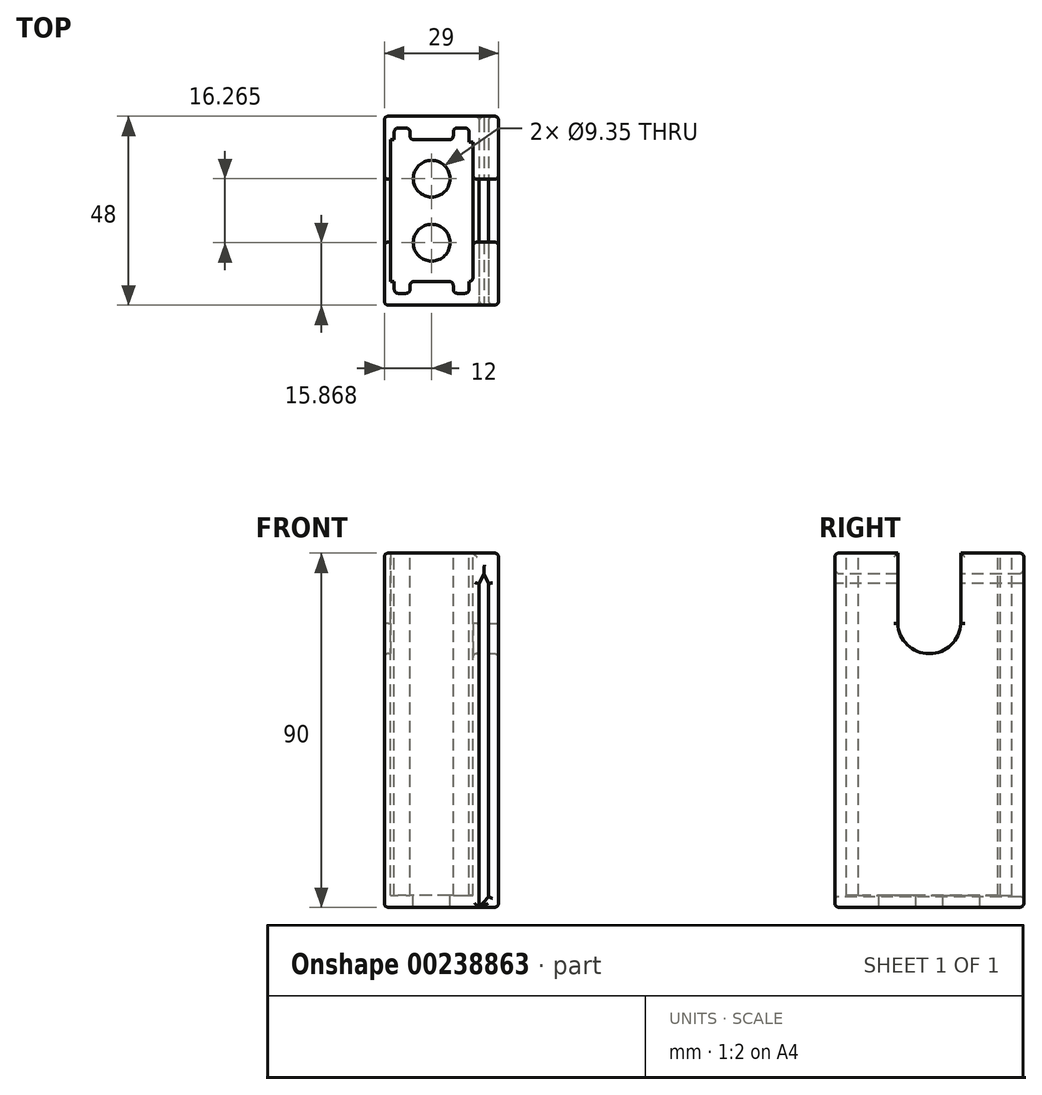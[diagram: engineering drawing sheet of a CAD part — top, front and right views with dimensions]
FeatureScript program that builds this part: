
annotation { "Feature Type Name" : "Feature", "Feature Type Description" : "" }
export const myFeature = defineFeature(function(context is Context, id is Id, definition is map)
    precondition{}
    {
        {
            var Q0;
            Q0=qCreatedBy(makeId("Right.planeOp"),FACE);
            var sketch = newSketch(context, id + "F0", { "sketchPlane" : qUnion([Q0])});
            skLineSegment(sketch, "E0", {"start": v(0, 0) * mm, "end": v(0, 45) * mm});
            skLineSegment(sketch, "E1", {"start": v(0, 45) * mm, "end": v(-24, 45) * mm});
            skLineSegment(sketch, "E2", {"start": v(-24, 45) * mm, "end": v(-24, 0) * mm});
            skLineSegment(sketch, "E3.MirrorCS", {"start": v(0, 45) * mm, "end": v(24, 45) * mm});
            skLineSegment(sketch, "E4.MirrorCS", {"start": v(24, 45) * mm, "end": v(24, 0) * mm});
            skLineSegment(sketch, "E5.MirrorCS", {"start": v(-24, -45) * mm, "end": v(-24, 0) * mm});
            skLineSegment(sketch, "E6.MirrorCS", {"start": v(0, -45) * mm, "end": v(-24, -45) * mm});
            skLineSegment(sketch, "E7.MirrorCS", {"start": v(0, -45) * mm, "end": v(24, -45) * mm});
            skLineSegment(sketch, "E8.MirrorCS", {"start": v(24, -45) * mm, "end": v(24, 0) * mm});
            skSolve(sketch);
        }
        {
            var Q0;
            Q0=makeQuery(id+"F0.imprint","IMPRINT",FACE,{"disambiguationData":[TD([[makeQuery(id+"F0.imprint","IMPRINT",EDGE,{"derivedFrom":sQuery(id+"F0.wireOp",EDGE,"E1")}),1.0]])]});
            extrude(context, id + "F1", {"entities" : qUnion([Q0]), "depth" : 24 * mm, "offsetDistance" : 25.4 * mm});
        }
        {
            var Q0;
            Q0=makeQuery(id+"F1.opExtrude","SWEPT_FACE",FACE,{"disambiguationData":[OSD([sQuery(id+"F0.wireOp",EDGE,"E1"),sQuery(id+"F0.wireOp",EDGE,"E3.MirrorCS")])]});
            var sketch = newSketch(context, id + "F2", { "sketchPlane" : qUnion([Q0])});
            skLineSegment(sketch, "E9", {"start": v(0, 10.58) * mm, "end": v(1.5, 10.58) * mm});
            skLineSegment(sketch, "E10", {"start": v(24, 10.58) * mm, "end": v(22.5, 10.58) * mm});
            skLineSegment(sketch, "E11", {"start": v(1.5, 0) * mm, "end": v(1.5, 18) * mm});
            skPoint(sketch, "E11.startSnap0", {"position": v(0, 0) * mm});
            skLineSegment(sketch, "E12.MirrorCS", {"start": v(1.5, 0) * mm, "end": v(1.5, -18) * mm});
            skLineSegment(sketch, "E13", {"start": v(1.5, 18) * mm, "end": v(22.5, 18) * mm});
            skLineSegment(sketch, "E14", {"start": v(22.5, 18) * mm, "end": v(22.5, -18) * mm});
            skLineSegment(sketch, "E15", {"start": v(22.5, -18) * mm, "end": v(1.5, -18) * mm});
            skLineSegment(sketch, "E16", {"start": v(22.5, 18) * mm, "end": v(20.97, 18) * mm});
            skLineSegment(sketch, "E17", {"start": v(22.5, 17.44) * mm, "end": v(21.5, 17.44) * mm});
            skLineSegment(sketch, "E18", {"start": v(21.5, 17.44) * mm, "end": v(17.5, 17.44) * mm});
            skLineSegment(sketch, "E19.MirrorCS", {"start": v(21.5, -17.44) * mm, "end": v(17.5, -17.44) * mm});
            skLineSegment(sketch, "E20", {"start": v(12, 18) * mm, "end": v(12, 7.15) * mm});
            skLineSegment(sketch, "E21.MirrorCS", {"start": v(2.5, -17.44) * mm, "end": v(6.5, -17.44) * mm});
            skLineSegment(sketch, "E22.MirrorCS", {"start": v(2.5, 17.44) * mm, "end": v(6.5, 17.44) * mm});
            skLineSegment(sketch, "E23", {"start": v(2.5, 0) * mm, "end": v(2.5, 21) * mm});
            skLineSegment(sketch, "E24", {"start": v(6.5, 18) * mm, "end": v(6.5, 21) * mm});
            skLineSegment(sketch, "E25", {"start": v(6.5, 21) * mm, "end": v(2.5, 21) * mm});
            skLineSegment(sketch, "E26.MirrorCS", {"start": v(21.5, 0) * mm, "end": v(21.5, 21) * mm});
            skLineSegment(sketch, "E27.MirrorCS", {"start": v(17.5, 21) * mm, "end": v(21.5, 21) * mm});
            skLineSegment(sketch, "E28.MirrorCS", {"start": v(17.5, 18) * mm, "end": v(17.5, 21) * mm});
            skLineSegment(sketch, "E29.MirrorCS", {"start": v(6.5, -21) * mm, "end": v(2.5, -21) * mm});
            skLineSegment(sketch, "E30.MirrorCS", {"start": v(6.5, -18) * mm, "end": v(6.5, -21) * mm});
            skLineSegment(sketch, "E31.MirrorCS", {"start": v(2.5, 0) * mm, "end": v(2.5, -21) * mm});
            skLineSegment(sketch, "E32.MirrorCS", {"start": v(17.5, -21) * mm, "end": v(21.5, -21) * mm});
            skLineSegment(sketch, "E33.MirrorCS", {"start": v(17.5, -18) * mm, "end": v(17.5, -21) * mm});
            skLineSegment(sketch, "E34.MirrorCS", {"start": v(21.5, 0) * mm, "end": v(21.5, -21) * mm});
            skSolve(sketch);
        }
        {
            var Q0;
            {var subQ0=sQuery(id+"F2.wireOp",EDGE,"E24");Q0=makeQuery(id+"F2.imprint","IMPRINT",FACE,{"disambiguationData":[TD([[makeQuery(id+"F2.imprint","IMPRINT",EDGE,{"derivedFrom":subQ0}),1.0]])]});}
            var Q1;
            {var subQ0=sQuery(id+"F2.wireOp",EDGE,"E27.MirrorCS");Q1=makeQuery(id+"F2.imprint","IMPRINT",FACE,{"disambiguationData":[TD([[makeQuery(id+"F2.imprint","IMPRINT",EDGE,{"derivedFrom":subQ0}),-1.0]])]});}
            var Q2;
            {var subQ2=sQuery(id+"F2.wireOp",EDGE,"E13");var subQ16=makeQuery(id+"F2.imprint","IMPRINT",VERTEX,{"derivedFrom":subQ2});Q2=makeQuery(id+"F2.imprint","IMPRINT",FACE,{"disambiguationData":[TD([[makeQuery(id+"F2.imprint","IMPRINT",EDGE,{"disambiguationData":[TD([[subQ16,1.0]])],"derivedFrom":subQ2}),-1.0]])]});}
            var Q3;
            {var subQ5=sQuery(id+"F2.wireOp",EDGE,"E12.MirrorCS");Q3=makeQuery(id+"F2.imprint","IMPRINT",FACE,{"disambiguationData":[TD([[makeQuery(id+"F2.imprint","IMPRINT",EDGE,{"derivedFrom":subQ5}),1.0]])]});}
            var Q4;
            {var subQ0=sQuery(id+"F2.wireOp",EDGE,"E17");Q4=makeQuery(id+"F2.imprint","IMPRINT",FACE,{"disambiguationData":[TD([[makeQuery(id+"F2.imprint","IMPRINT",EDGE,{"derivedFrom":subQ0}),1.0]])]});}
            var Q5;
            {var subQ4=sQuery(id+"F2.wireOp",EDGE,"E32.MirrorCS");Q5=makeQuery(id+"F2.imprint","IMPRINT",FACE,{"disambiguationData":[TD([[makeQuery(id+"F2.imprint","IMPRINT",EDGE,{"derivedFrom":subQ4}),1.0]])]});}
            var Q6;
            {var subQ4=sQuery(id+"F2.wireOp",EDGE,"E29.MirrorCS");Q6=makeQuery(id+"F2.imprint","IMPRINT",FACE,{"disambiguationData":[TD([[makeQuery(id+"F2.imprint","IMPRINT",EDGE,{"derivedFrom":subQ4}),-1.0]])]});}
            extrude(context, id + "F3", {"entities" : qUnion([Q0, Q1, Q2, Q3, Q4, Q5, Q6]), "operationType" : NewBodyOperationType.REMOVE, "oppositeDirection" : true, "depth" : 87 * mm, "offsetDistance" : 25.4 * mm});
        }
        {
            var Q0;
            Q0=makeQuery(id+"F1.opExtrude","CAP_FACE",FACE,{"disambiguationData":[OSD([sQuery(id+"F0.wireOp",EDGE,"E1"),sQuery(id+"F0.wireOp",EDGE,"E2"),sQuery(id+"F0.wireOp",EDGE,"E3.MirrorCS"),sQuery(id+"F0.wireOp",EDGE,"E4.MirrorCS"),sQuery(id+"F0.wireOp",EDGE,"E5.MirrorCS"),sQuery(id+"F0.wireOp",EDGE,"E6.MirrorCS"),sQuery(id+"F0.wireOp",EDGE,"E7.MirrorCS"),sQuery(id+"F0.wireOp",EDGE,"E8.MirrorCS")])],"isStart":false});
            var sketch = newSketch(context, id + "F4", { "sketchPlane" : qUnion([Q0])});
            skLineSegment(sketch, "E35", {"start": v(0, 45) * mm, "end": v(0, 27.46) * mm});
            skLineSegment(sketch, "E36", {"start": v(0, 45) * mm, "end": v(-8, 45) * mm});
            skLineSegment(sketch, "E37", {"start": v(-8, 45) * mm, "end": v(-8, 27.14) * mm});
            skCircle(sketch, "E38", {"center": v(0, 27.46) * mm, "radius": 8 * mm});
            skLineSegment(sketch, "E39.MirrorCS", {"start": v(0, 45) * mm, "end": v(8, 45) * mm});
            skLineSegment(sketch, "E40.MirrorCS", {"start": v(8, 45) * mm, "end": v(8, 27.14) * mm});
            skSolve(sketch);
        }
        {
            var Q0;
            {var subQ0=sQuery(id+"F4.wireOp",EDGE,"E39.MirrorCS");Q0=makeQuery(id+"F4.imprint","IMPRINT",FACE,{"disambiguationData":[TD([[makeQuery(id+"F4.imprint","IMPRINT",EDGE,{"derivedFrom":subQ0}),-1.0]])]});}
            var Q1;
            {var subQ0=sQuery(id+"F4.wireOp",EDGE,"E36");Q1=makeQuery(id+"F4.imprint","IMPRINT",FACE,{"disambiguationData":[TD([[makeQuery(id+"F4.imprint","IMPRINT",EDGE,{"derivedFrom":subQ0}),-1.0]])]});}
            var Q2;
            {var subQ0=sQuery(id+"F4.wireOp",EDGE,"E38");var subQ1=sQuery(id+"F4.wireOp",EDGE,"E37");var subQ2=makeQuery(id+"F4.imprint","INTERSECT",VERTEX,{"disambiguationData":[OD(0.0)],"derivedFrom":[subQ1,subQ0]});Q2=makeQuery(id+"F4.imprint","IMPRINT",FACE,{"disambiguationData":[TD([[makeQuery(id+"F4.imprint","IMPRINT",EDGE,{"disambiguationData":[TD([[subQ2,1.0]])],"derivedFrom":subQ1}),1.0]])]});}
            extrude(context, id + "F5", {"entities" : qUnion([Q0, Q1, Q2]), "operationType" : NewBodyOperationType.REMOVE, "oppositeDirection" : true, "depth" : 25.4 * mm, "offsetDistance" : 25.4 * mm});
        }
        {
            var Q0;
            Q0=makeQuery(id+"F1.opExtrude","CAP_FACE",FACE,{"disambiguationData":[OSD([sQuery(id+"F0.wireOp",EDGE,"E1"),sQuery(id+"F0.wireOp",EDGE,"E2"),sQuery(id+"F0.wireOp",EDGE,"E3.MirrorCS"),sQuery(id+"F0.wireOp",EDGE,"E4.MirrorCS"),sQuery(id+"F0.wireOp",EDGE,"E5.MirrorCS"),sQuery(id+"F0.wireOp",EDGE,"E6.MirrorCS"),sQuery(id+"F0.wireOp",EDGE,"E7.MirrorCS"),sQuery(id+"F0.wireOp",EDGE,"E8.MirrorCS")])],"isStart":false});
            extrude(context, id + "F6", {"entities" : qUnion([Q0]), "operationType" : NewBodyOperationType.ADD, "depth" : 5 * mm, "offsetDistance" : 25.4 * mm});
        }
        {
            var Q0;
            {var subQ0=sQuery(id+"F0.wireOp",EDGE,"E5.MirrorCS");var subQ1=sQuery(id+"F0.wireOp",EDGE,"E2");Q0=makeQuery(id+"F6.boolean.opBoolean","MERGE",FACE,{"derivedFrom":[makeQuery(id+"F1.opExtrude","SWEPT_FACE",FACE,{"disambiguationData":[OSD([subQ1,subQ0])]}),makeQuery(id+"F6.opExtrude","SWEPT_FACE",FACE,{"disambiguationData":[OSD([subQ1,subQ0])]})]});}
            var sketch = newSketch(context, id + "F7", { "sketchPlane" : qUnion([Q0])});
            skLineSegment(sketch, "E41", {"start": v(29, 37.24) * mm, "end": v(24, 37.24) * mm});
            skLineSegment(sketch, "E42", {"start": v(24, 37.24) * mm, "end": v(24, -45) * mm});
            skLineSegment(sketch, "E43", {"start": v(26.5, 37.24) * mm, "end": v(26.5, -45) * mm});
            skLineSegment(sketch, "E44", {"start": v(24.09, -45) * mm, "end": v(26.5, -42.37) * mm});
            skLineSegment(sketch, "E45", {"start": v(25.33, 39.72) * mm, "end": v(24, 37.24) * mm});
            skLineSegment(sketch, "E46", {"start": v(25.33, 39.72) * mm, "end": v(26.5, 37.24) * mm});
            skSolve(sketch);
        }
        {
            var Q0;
            {var subQ4=sQuery(id+"F7.wireOp",EDGE,"E42");Q0=makeQuery(id+"F7.imprint","IMPRINT",FACE,{"disambiguationData":[TD([[makeQuery(id+"F7.imprint","IMPRINT",EDGE,{"derivedFrom":subQ4}),1.0]])]});}
            var Q1;
            {var subQ0=sQuery(id+"F7.wireOp",EDGE,"E45");Q1=makeQuery(id+"F7.imprint","IMPRINT",FACE,{"disambiguationData":[TD([[makeQuery(id+"F7.imprint","IMPRINT",EDGE,{"derivedFrom":subQ0}),1.0]])]});}
            extrude(context, id + "F8", {"entities" : qUnion([Q0, Q1]), "operationType" : NewBodyOperationType.REMOVE, "oppositeDirection" : true, "depth" : 127 * mm, "offsetDistance" : 25.4 * mm});
        }
        {
            var Q0;
            Q0=makeQuery(id+"F6.opExtrude","CAP_EDGE",EDGE,{"disambiguationData":[OSD([sQuery(id+"F0.wireOp",EDGE,"E4.MirrorCS"),sQuery(id+"F0.wireOp",EDGE,"E8.MirrorCS")])],"isStart":false});
            var Q1;
            Q1=makeQuery(id+"F6.opExtrude","CAP_EDGE",EDGE,{"disambiguationData":[OSD([sQuery(id+"F0.wireOp",EDGE,"E2"),sQuery(id+"F0.wireOp",EDGE,"E5.MirrorCS")])],"isStart":false});
            var Q2;
            Q2=makeQuery(id+"F6.opExtrude","CAP_FACE",FACE,{"disambiguationData":[OSD([sQuery(id+"F0.wireOp",EDGE,"E1"),sQuery(id+"F0.wireOp",EDGE,"E2"),sQuery(id+"F0.wireOp",EDGE,"E3.MirrorCS"),sQuery(id+"F0.wireOp",EDGE,"E4.MirrorCS"),sQuery(id+"F0.wireOp",EDGE,"E5.MirrorCS"),sQuery(id+"F0.wireOp",EDGE,"E6.MirrorCS"),sQuery(id+"F0.wireOp",EDGE,"E7.MirrorCS"),sQuery(id+"F0.wireOp",EDGE,"E8.MirrorCS")])],"isStart":false});
            var Q3;
            {var subQ0=sQuery(id+"F0.wireOp",EDGE,"E8.MirrorCS");var subQ1=sQuery(id+"F0.wireOp",EDGE,"E4.MirrorCS");Q3=makeQuery(id+"F6.boolean.opBoolean","MERGE",FACE,{"derivedFrom":[makeQuery(id+"F1.opExtrude","SWEPT_FACE",FACE,{"disambiguationData":[OSD([subQ1,subQ0])]}),makeQuery(id+"F6.opExtrude","SWEPT_FACE",FACE,{"disambiguationData":[OSD([subQ1,subQ0])]})]});}
            var Q4;
            Q4=makeQuery(id+"F1.opExtrude","CAP_FACE",FACE,{"disambiguationData":[OSD([sQuery(id+"F0.wireOp",EDGE,"E1"),sQuery(id+"F0.wireOp",EDGE,"E2"),sQuery(id+"F0.wireOp",EDGE,"E3.MirrorCS"),sQuery(id+"F0.wireOp",EDGE,"E4.MirrorCS"),sQuery(id+"F0.wireOp",EDGE,"E5.MirrorCS"),sQuery(id+"F0.wireOp",EDGE,"E6.MirrorCS"),sQuery(id+"F0.wireOp",EDGE,"E7.MirrorCS"),sQuery(id+"F0.wireOp",EDGE,"E8.MirrorCS")])],"isStart":true});
            var Q5;
            {var subQ0=sQuery(id+"F0.wireOp",EDGE,"E5.MirrorCS");var subQ1=sQuery(id+"F0.wireOp",EDGE,"E2");Q5=makeQuery(id+"F6.boolean.opBoolean","MERGE",FACE,{"derivedFrom":[makeQuery(id+"F1.opExtrude","SWEPT_FACE",FACE,{"disambiguationData":[OSD([subQ1,subQ0])]}),makeQuery(id+"F6.opExtrude","SWEPT_FACE",FACE,{"disambiguationData":[OSD([subQ1,subQ0])]})]});}
            var Q6;
            Q6=makeQuery(id+"F3.boolean.opBoolean","COPY",EDGE,{"derivedFrom":makeQuery(id+"F3.opExtrude","SWEPT_EDGE",EDGE,{"disambiguationData":[OSD([sQuery(id+"F2.wireOp",EDGE,"E26.MirrorCS"),sQuery(id+"F2.wireOp",EDGE,"E27.MirrorCS")])]})});
            var Q7;
            Q7=makeQuery(id+"F3.boolean.opBoolean","COPY",EDGE,{"derivedFrom":makeQuery(id+"F3.opExtrude","SWEPT_EDGE",EDGE,{"disambiguationData":[OSD([sQuery(id+"F2.wireOp",EDGE,"E27.MirrorCS"),sQuery(id+"F2.wireOp",EDGE,"E28.MirrorCS")])]})});
            var Q8;
            Q8=makeQuery(id+"F3.boolean.opBoolean","COPY",EDGE,{"derivedFrom":makeQuery(id+"F3.opExtrude","SWEPT_EDGE",EDGE,{"disambiguationData":[OSD([sQuery(id+"F2.wireOp",EDGE,"E23"),sQuery(id+"F2.wireOp",EDGE,"E25")])]})});
            var Q9;
            Q9=makeQuery(id+"F3.boolean.opBoolean","COPY",EDGE,{"derivedFrom":makeQuery(id+"F3.opExtrude","SWEPT_EDGE",EDGE,{"disambiguationData":[OSD([sQuery(id+"F2.wireOp",EDGE,"E24"),sQuery(id+"F2.wireOp",EDGE,"E25")])]})});
            var Q10;
            Q10=makeQuery(id+"F3.boolean.opBoolean","COPY",EDGE,{"derivedFrom":makeQuery(id+"F3.opExtrude","SWEPT_EDGE",EDGE,{"disambiguationData":[OSD([sQuery(id+"F2.wireOp",EDGE,"E13"),sQuery(id+"F2.wireOp",EDGE,"E28.MirrorCS")])]})});
            var Q11;
            Q11=makeQuery(id+"F3.boolean.opBoolean","COPY",EDGE,{"derivedFrom":makeQuery(id+"F3.opExtrude","SWEPT_EDGE",EDGE,{"disambiguationData":[OSD([sQuery(id+"F2.wireOp",EDGE,"E13"),sQuery(id+"F2.wireOp",EDGE,"E24")])]})});
            var Q12;
            Q12=makeQuery(id+"F3.boolean.opBoolean","COPY",EDGE,{"derivedFrom":makeQuery(id+"F3.opExtrude","SWEPT_EDGE",EDGE,{"disambiguationData":[OSD([sQuery(id+"F2.wireOp",EDGE,"E32.MirrorCS"),sQuery(id+"F2.wireOp",EDGE,"E34.MirrorCS")])]})});
            var Q13;
            Q13=makeQuery(id+"F3.boolean.opBoolean","COPY",EDGE,{"derivedFrom":makeQuery(id+"F3.opExtrude","SWEPT_EDGE",EDGE,{"disambiguationData":[OSD([sQuery(id+"F2.wireOp",EDGE,"E14"),sQuery(id+"F2.wireOp",EDGE,"E15")])]})});
            var Q14;
            Q14=makeQuery(id+"F3.boolean.opBoolean","COPY",EDGE,{"derivedFrom":makeQuery(id+"F3.opExtrude","SWEPT_EDGE",EDGE,{"disambiguationData":[OSD([sQuery(id+"F2.wireOp",EDGE,"E15"),sQuery(id+"F2.wireOp",EDGE,"E33.MirrorCS")])]})});
            var Q15;
            Q15=makeQuery(id+"F3.boolean.opBoolean","COPY",EDGE,{"derivedFrom":makeQuery(id+"F3.opExtrude","SWEPT_EDGE",EDGE,{"disambiguationData":[OSD([sQuery(id+"F2.wireOp",EDGE,"E32.MirrorCS"),sQuery(id+"F2.wireOp",EDGE,"E33.MirrorCS")])]})});
            var Q16;
            Q16=makeQuery(id+"F3.boolean.opBoolean","COPY",EDGE,{"derivedFrom":makeQuery(id+"F3.opExtrude","SWEPT_EDGE",EDGE,{"disambiguationData":[OSD([sQuery(id+"F2.wireOp",EDGE,"E15"),sQuery(id+"F2.wireOp",EDGE,"E30.MirrorCS")])]})});
            var Q17;
            Q17=makeQuery(id+"F3.boolean.opBoolean","COPY",EDGE,{"derivedFrom":makeQuery(id+"F3.opExtrude","SWEPT_EDGE",EDGE,{"disambiguationData":[OSD([sQuery(id+"F2.wireOp",EDGE,"E29.MirrorCS"),sQuery(id+"F2.wireOp",EDGE,"E30.MirrorCS")])]})});
            var Q18;
            Q18=makeQuery(id+"F3.boolean.opBoolean","COPY",EDGE,{"derivedFrom":makeQuery(id+"F3.opExtrude","SWEPT_EDGE",EDGE,{"disambiguationData":[OSD([sQuery(id+"F2.wireOp",EDGE,"E29.MirrorCS"),sQuery(id+"F2.wireOp",EDGE,"E31.MirrorCS")])]})});
            var Q19;
            {var subQ0=sQuery(id+"F2.wireOp",EDGE,"E15");Q19=makeQuery(id+"F3.boolean.opBoolean","COPY",EDGE,{"derivedFrom":makeQuery(id+"F3.opExtrude","CAP_EDGE",EDGE,{"disambiguationData":[OSD([subQ0]),TDD([makeQuery(id+"F2.imprint","IMPRINT",EDGE,{"disambiguationData":[TD([[makeQuery(id+"F2.imprint","INTERSECT",VERTEX,{"derivedFrom":[subQ0,sQuery(id+"F2.wireOp",EDGE,"E30.MirrorCS")]}),1.0]])],"derivedFrom":subQ0})])],"isStart":true})});}
            var Q20;
            {var subQ0=sQuery(id+"F2.wireOp",EDGE,"E14");Q20=makeQuery(id+"F5.boolean.opBoolean","SPLIT",EDGE,{"disambiguationData":[TD([makeQuery(id+"F5.opExtrude","SWEPT_FACE",FACE,{"disambiguationData":[OSD([sQuery(id+"F4.wireOp",EDGE,"E37")])]})])],"derivedFrom":makeQuery(id+"F3.boolean.opBoolean","COPY",EDGE,{"derivedFrom":makeQuery(id+"F3.opExtrude","CAP_EDGE",EDGE,{"disambiguationData":[OSD([subQ0])],"isStart":true})})});}
            var Q21;
            Q21=makeQuery(id+"F3.boolean.opBoolean","COPY",EDGE,{"derivedFrom":makeQuery(id+"F3.opExtrude","CAP_EDGE",EDGE,{"disambiguationData":[OSD([sQuery(id+"F2.wireOp",EDGE,"E34.MirrorCS")])],"isStart":true})});
            var Q22;
            Q22=makeQuery(id+"F3.boolean.opBoolean","COPY",EDGE,{"derivedFrom":makeQuery(id+"F3.opExtrude","CAP_EDGE",EDGE,{"disambiguationData":[OSD([sQuery(id+"F2.wireOp",EDGE,"E33.MirrorCS")])],"isStart":true})});
            var Q23;
            Q23=makeQuery(id+"F3.boolean.opBoolean","COPY",EDGE,{"derivedFrom":makeQuery(id+"F3.opExtrude","CAP_EDGE",EDGE,{"disambiguationData":[OSD([sQuery(id+"F2.wireOp",EDGE,"E30.MirrorCS")])],"isStart":true})});
            var Q24;
            Q24=makeQuery(id+"F3.boolean.opBoolean","COPY",EDGE,{"derivedFrom":makeQuery(id+"F3.opExtrude","CAP_EDGE",EDGE,{"disambiguationData":[OSD([sQuery(id+"F2.wireOp",EDGE,"E31.MirrorCS")])],"isStart":true})});
            var Q25;
            Q25=makeQuery(id+"F3.boolean.opBoolean","COPY",EDGE,{"derivedFrom":makeQuery(id+"F3.opExtrude","CAP_EDGE",EDGE,{"disambiguationData":[OSD([sQuery(id+"F2.wireOp",EDGE,"E24")])],"isStart":true})});
            var Q26;
            Q26=makeQuery(id+"F3.boolean.opBoolean","COPY",EDGE,{"derivedFrom":makeQuery(id+"F3.opExtrude","CAP_EDGE",EDGE,{"disambiguationData":[OSD([sQuery(id+"F2.wireOp",EDGE,"E26.MirrorCS")])],"isStart":true})});
            var Q27;
            Q27=makeQuery(id+"F3.boolean.opBoolean","COPY",EDGE,{"derivedFrom":makeQuery(id+"F3.opExtrude","CAP_EDGE",EDGE,{"disambiguationData":[OSD([sQuery(id+"F2.wireOp",EDGE,"E28.MirrorCS")])],"isStart":true})});
            var Q28;
            Q28=makeQuery(id+"F3.boolean.opBoolean","COPY",EDGE,{"derivedFrom":makeQuery(id+"F3.opExtrude","CAP_EDGE",EDGE,{"disambiguationData":[OSD([sQuery(id+"F2.wireOp",EDGE,"E27.MirrorCS")])],"isStart":true})});
            var Q29;
            Q29=makeQuery(id+"F3.boolean.opBoolean","COPY",EDGE,{"derivedFrom":makeQuery(id+"F3.opExtrude","CAP_EDGE",EDGE,{"disambiguationData":[OSD([sQuery(id+"F2.wireOp",EDGE,"E25")])],"isStart":true})});
            var Q30;
            Q30=makeQuery(id+"F3.boolean.opBoolean","COPY",EDGE,{"derivedFrom":makeQuery(id+"F3.opExtrude","CAP_EDGE",EDGE,{"disambiguationData":[OSD([sQuery(id+"F2.wireOp",EDGE,"E23")])],"isStart":true})});
            var Q31;
            {var subQ0=sQuery(id+"F4.wireOp",EDGE,"E40.MirrorCS");var subQ1=sQuery(id+"F4.wireOp",EDGE,"E39.MirrorCS");var subQ2=sQuery(id+"F0.wireOp",EDGE,"E3.MirrorCS");var subQ3=sQuery(id+"F0.wireOp",EDGE,"E1");Q31=makeQuery(id+"F6.boolean.opBoolean","MERGE",EDGE,{"derivedFrom":[makeQuery(id+"F5.boolean.opBoolean","COPY",EDGE,{"disambiguationData":[TD([makeQuery(id+"F3.boolean.opBoolean","COPY",FACE,{"derivedFrom":makeQuery(id+"F3.opExtrude","SWEPT_FACE",FACE,{"disambiguationData":[OSD([sQuery(id+"F2.wireOp",EDGE,"E14")])]})})])],"derivedFrom":makeQuery(id+"F5.opExtrude","SWEPT_EDGE",EDGE,{"disambiguationData":[OSD([subQ3,subQ2,subQ1,subQ0])]})}),makeQuery(id+"F6.opExtrude","SWEPT_EDGE",EDGE,{"disambiguationData":[OSD([subQ3,subQ2,subQ1,subQ0])]})]});}
            var Q32;
            {var subQ0=sQuery(id+"F4.wireOp",EDGE,"E37");var subQ1=sQuery(id+"F4.wireOp",EDGE,"E36");var subQ2=sQuery(id+"F0.wireOp",EDGE,"E3.MirrorCS");var subQ3=sQuery(id+"F0.wireOp",EDGE,"E1");Q32=makeQuery(id+"F6.boolean.opBoolean","MERGE",EDGE,{"derivedFrom":[makeQuery(id+"F5.boolean.opBoolean","COPY",EDGE,{"disambiguationData":[TD([makeQuery(id+"F3.boolean.opBoolean","COPY",FACE,{"derivedFrom":makeQuery(id+"F3.opExtrude","SWEPT_FACE",FACE,{"disambiguationData":[OSD([sQuery(id+"F2.wireOp",EDGE,"E14")])]})})])],"derivedFrom":makeQuery(id+"F5.opExtrude","SWEPT_EDGE",EDGE,{"disambiguationData":[OSD([subQ3,subQ2,subQ1,subQ0])]})}),makeQuery(id+"F6.opExtrude","SWEPT_EDGE",EDGE,{"disambiguationData":[OSD([subQ3,subQ2,subQ1,subQ0])]})]});}
            var Q33;
            {var subQ0=sQuery(id+"F2.wireOp",EDGE,"E14");Q33=makeQuery(id+"F5.boolean.opBoolean","SPLIT",EDGE,{"disambiguationData":[TD([makeQuery(id+"F3.boolean.opBoolean","COPY",FACE,{"derivedFrom":makeQuery(id+"F3.opExtrude","SWEPT_FACE",FACE,{"disambiguationData":[OSD([sQuery(id+"F2.wireOp",EDGE,"E17")])]})})])],"derivedFrom":makeQuery(id+"F3.boolean.opBoolean","COPY",EDGE,{"derivedFrom":makeQuery(id+"F3.opExtrude","CAP_EDGE",EDGE,{"disambiguationData":[OSD([subQ0])],"isStart":true})})});}
            var Q34;
            Q34=makeQuery(id+"F5.boolean.opBoolean","INTERSECT",EDGE,{"derivedFrom":[makeQuery(id+"F3.boolean.opBoolean","COPY",FACE,{"derivedFrom":makeQuery(id+"F3.opExtrude","SWEPT_FACE",FACE,{"disambiguationData":[OSD([sQuery(id+"F2.wireOp",EDGE,"E14")])]})}),makeQuery(id+"F5.opExtrude","SWEPT_FACE",FACE,{"disambiguationData":[OSD([sQuery(id+"F4.wireOp",EDGE,"E40.MirrorCS")])]})]});
            var Q35;
            Q35=makeQuery(id+"F5.boolean.opBoolean","INTERSECT",EDGE,{"derivedFrom":[makeQuery(id+"F3.boolean.opBoolean","COPY",FACE,{"derivedFrom":makeQuery(id+"F3.opExtrude","SWEPT_FACE",FACE,{"disambiguationData":[OSD([sQuery(id+"F2.wireOp",EDGE,"E14")])]})}),makeQuery(id+"F5.opExtrude","SWEPT_FACE",FACE,{"disambiguationData":[OSD([sQuery(id+"F4.wireOp",EDGE,"E38")])]})]});
            var Q36;
            Q36=makeQuery(id+"F5.boolean.opBoolean","INTERSECT",EDGE,{"derivedFrom":[makeQuery(id+"F3.boolean.opBoolean","COPY",FACE,{"derivedFrom":makeQuery(id+"F3.opExtrude","SWEPT_FACE",FACE,{"disambiguationData":[OSD([sQuery(id+"F2.wireOp",EDGE,"E14")])]})}),makeQuery(id+"F5.opExtrude","SWEPT_FACE",FACE,{"disambiguationData":[OSD([sQuery(id+"F4.wireOp",EDGE,"E37")])]})]});
            fillet(context, id + "F9", {"entities" : qUnion([Q0, Q1, Q2, Q3, Q4, Q5, Q6, Q7, Q8, Q9, Q10, Q11, Q12, Q13, Q14, Q15, Q16, Q17, Q18, Q19, Q20, Q21, Q22, Q23, Q24, Q25, Q26, Q27, Q28, Q29, Q30, Q31, Q32, Q33, Q34, Q35, Q36]), "radius" : 1 * mm, "tangentPropagation" : true, "allowEdgeOverflow" : false});
        }
        {
            var Q0;
            Q0=makeQuery(id+"F3.boolean.opBoolean","COPY",FACE,{"derivedFrom":makeQuery(id+"F3.opExtrude","CAP_FACE",FACE,{"disambiguationData":[OSD([sQuery(id+"F2.wireOp",EDGE,"E11"),sQuery(id+"F2.wireOp",EDGE,"E12.MirrorCS"),sQuery(id+"F2.wireOp",EDGE,"E13"),sQuery(id+"F2.wireOp",EDGE,"E14"),sQuery(id+"F2.wireOp",EDGE,"E15"),sQuery(id+"F2.wireOp",EDGE,"E17"),sQuery(id+"F2.wireOp",EDGE,"E23"),sQuery(id+"F2.wireOp",EDGE,"E24"),sQuery(id+"F2.wireOp",EDGE,"E25"),sQuery(id+"F2.wireOp",EDGE,"E26.MirrorCS"),sQuery(id+"F2.wireOp",EDGE,"E27.MirrorCS"),sQuery(id+"F2.wireOp",EDGE,"E28.MirrorCS"),sQuery(id+"F2.wireOp",EDGE,"E29.MirrorCS"),sQuery(id+"F2.wireOp",EDGE,"E30.MirrorCS"),sQuery(id+"F2.wireOp",EDGE,"E31.MirrorCS"),sQuery(id+"F2.wireOp",EDGE,"E32.MirrorCS"),sQuery(id+"F2.wireOp",EDGE,"E33.MirrorCS"),sQuery(id+"F2.wireOp",EDGE,"E34.MirrorCS")])],"isStart":false})});
            var sketch = newSketch(context, id + "F10", { "sketchPlane" : qUnion([Q0])});
            skLineSegment(sketch, "E47", {"start": v(12, 18) * mm, "end": v(12, -20.67) * mm});
            skLineSegment(sketch, "E48", {"start": v(22.5, -7.82) * mm, "end": v(12, -7.82) * mm});
            skLineSegment(sketch, "E49", {"start": v(22.5, 8.13) * mm, "end": v(12, 8.13) * mm});
            skCircle(sketch, "E50", {"center": v(12, 8.13) * mm, "radius": 4.67 * mm});
            skCircle(sketch, "E51.MirrorC", {"center": v(12, -8.13) * mm, "radius": 4.67 * mm});
            skSolve(sketch);
        }
        {
            var Q0;
            {var subQ0=sQuery(id+"F10.wireOp",EDGE,"E47");var subQ1=makeQuery(id+"F10.imprint","INTERSECT",VERTEX,{"derivedFrom":[subQ0,sQuery(id+"F10.wireOp",EDGE,"E49")]});Q0=makeQuery(id+"F10.imprint","IMPRINT",FACE,{"disambiguationData":[TD([[makeQuery(id+"F10.imprint","IMPRINT",EDGE,{"disambiguationData":[TD([[subQ1,1.0]])],"derivedFrom":subQ0}),-1.0]])]});}
            var Q1;
            {var subQ0=sQuery(id+"F10.wireOp",EDGE,"E49");var subQ1=sQuery(id+"F10.wireOp",EDGE,"E47");var subQ2=makeQuery(id+"F10.imprint","INTERSECT",VERTEX,{"derivedFrom":[subQ1,subQ0]});Q1=makeQuery(id+"F10.imprint","IMPRINT",FACE,{"disambiguationData":[TD([[makeQuery(id+"F10.imprint","IMPRINT",EDGE,{"disambiguationData":[TD([[subQ2,-1.0]])],"derivedFrom":subQ1}),1.0]])]});}
            var Q2;
            {var subQ0=sQuery(id+"F10.wireOp",EDGE,"E49");var subQ1=sQuery(id+"F10.wireOp",EDGE,"E47");var subQ2=makeQuery(id+"F10.imprint","INTERSECT",VERTEX,{"derivedFrom":[subQ1,subQ0]});Q2=makeQuery(id+"F10.imprint","IMPRINT",FACE,{"disambiguationData":[TD([[makeQuery(id+"F10.imprint","IMPRINT",EDGE,{"disambiguationData":[TD([[subQ2,1.0]])],"derivedFrom":subQ1}),1.0]])]});}
            var Q3;
            {var subQ0=sQuery(id+"F10.wireOp",EDGE,"E47");var subQ1=makeQuery(id+"F10.imprint","INTERSECT",VERTEX,{"derivedFrom":[subQ0,sQuery(id+"F10.wireOp",EDGE,"E48")]});Q3=makeQuery(id+"F10.imprint","IMPRINT",FACE,{"disambiguationData":[TD([[makeQuery(id+"F10.imprint","IMPRINT",EDGE,{"disambiguationData":[TD([[subQ1,1.0]])],"derivedFrom":subQ0}),-1.0]])]});}
            var Q4;
            {var subQ0=sQuery(id+"F10.wireOp",EDGE,"E48");var subQ1=sQuery(id+"F10.wireOp",EDGE,"E47");var subQ2=makeQuery(id+"F10.imprint","INTERSECT",VERTEX,{"derivedFrom":[subQ1,subQ0]});Q4=makeQuery(id+"F10.imprint","IMPRINT",FACE,{"disambiguationData":[TD([[makeQuery(id+"F10.imprint","IMPRINT",EDGE,{"disambiguationData":[TD([[subQ2,1.0]])],"derivedFrom":subQ1}),1.0]])]});}
            var Q5;
            {var subQ0=sQuery(id+"F10.wireOp",EDGE,"E48");var subQ1=sQuery(id+"F10.wireOp",EDGE,"E47");var subQ2=makeQuery(id+"F10.imprint","INTERSECT",VERTEX,{"derivedFrom":[subQ1,subQ0]});Q5=makeQuery(id+"F10.imprint","IMPRINT",FACE,{"disambiguationData":[TD([[makeQuery(id+"F10.imprint","IMPRINT",EDGE,{"disambiguationData":[TD([[subQ2,-1.0]])],"derivedFrom":subQ1}),1.0]])]});}
            extrude(context, id + "F11", {"entities" : qUnion([Q0, Q1, Q2, Q3, Q4, Q5]), "operationType" : NewBodyOperationType.REMOVE, "oppositeDirection" : true, "depth" : 25.4 * mm, "offsetDistance" : 25.4 * mm});
        }
    });
